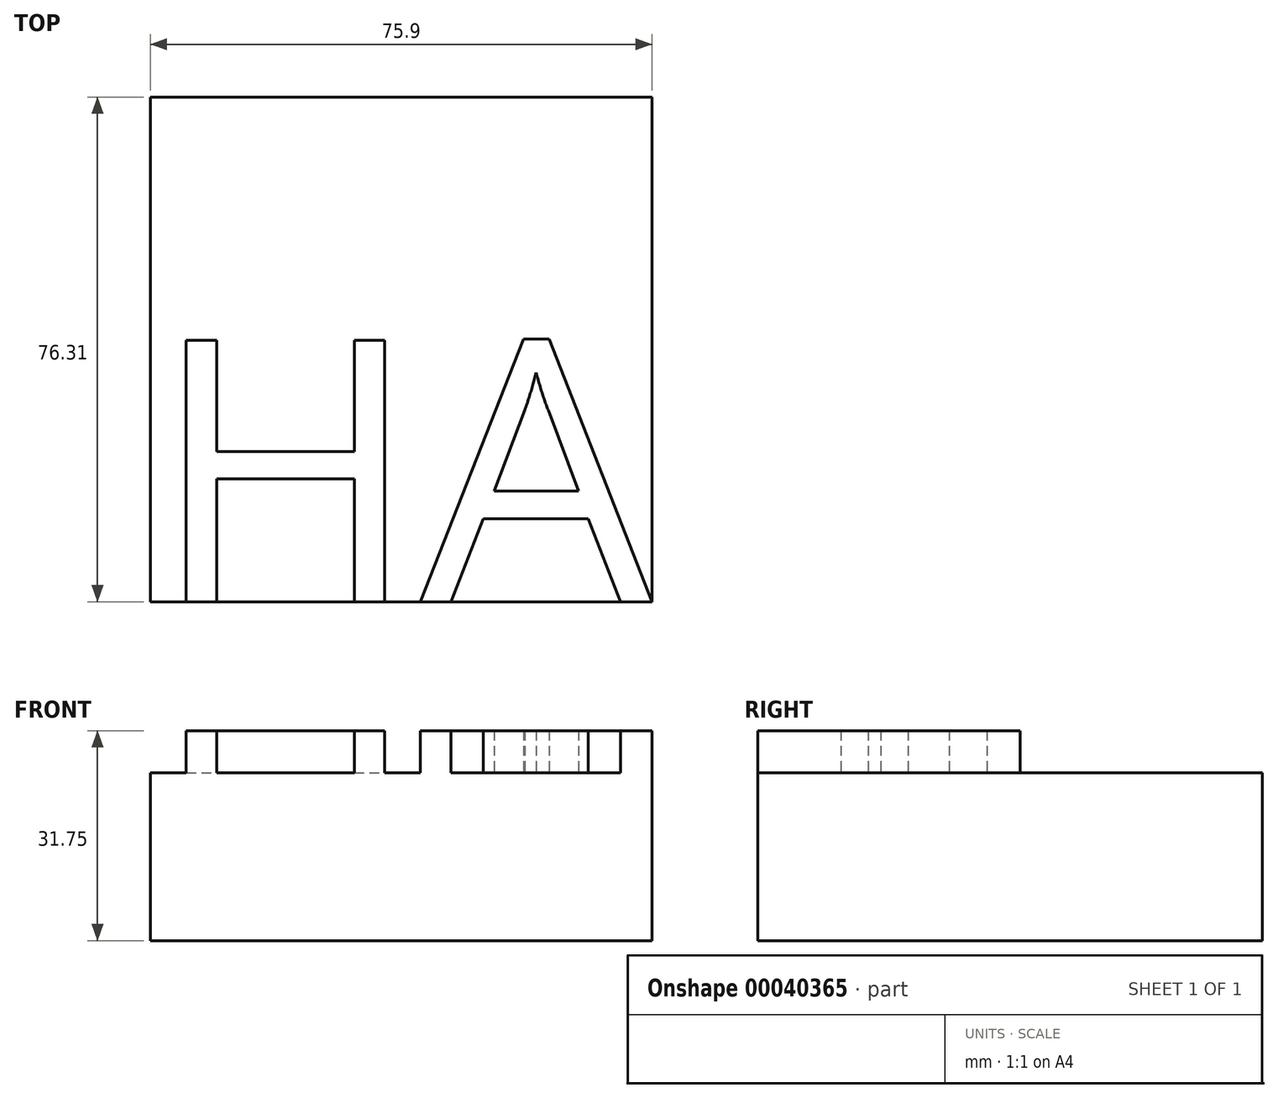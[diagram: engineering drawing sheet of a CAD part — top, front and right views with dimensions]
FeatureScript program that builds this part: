
annotation { "Feature Type Name" : "Feature", "Feature Type Description" : "" }
export const myFeature = defineFeature(function(context is Context, id is Id, definition is map)
    precondition{}
    {
        {
            var Q0;
            Q0=qCreatedBy(makeId("Top.planeOp"),FACE);
            var sketch = newSketch(context, id + "F0", { "sketchPlane" : qUnion([Q0])});
            skLineSegment(sketch, "E0.bottom", {"start": v(0, 0) * mm, "end": v(-75.9, 0) * mm});
            skLineSegment(sketch, "E0.top", {"start": v(0, 76.31) * mm, "end": v(-75.9, 76.31) * mm});
            skLineSegment(sketch, "E0.left", {"start": v(0, 0) * mm, "end": v(0, 76.31) * mm});
            skLineSegment(sketch, "E0.right", {"start": v(-75.9, 0) * mm, "end": v(-75.9, 76.31) * mm});
            skSolve(sketch);
        }
        {
            var Q0;
            Q0=makeQuery(id+"F0.imprint","IMPRINT",FACE,{"disambiguationData":[TD([[makeQuery(id+"F0.imprint","IMPRINT",EDGE,{"derivedFrom":sQuery(id+"F0.wireOp",EDGE,"E0.bottom")}),-1.0]])]});
            extrude(context, id + "F1", {"entities" : qUnion([Q0]), "depth" : 25.4 * mm});
        }
        {
            var Q0;
            Q0=makeQuery(id+"F1.opExtrude","CAP_FACE",FACE,{"disambiguationData":[OSD([sQuery(id+"F0.wireOp",EDGE,"E0.bottom"),sQuery(id+"F0.wireOp",EDGE,"E0.top"),sQuery(id+"F0.wireOp",EDGE,"E0.left"),sQuery(id+"F0.wireOp",EDGE,"E0.right")])],"isStart":false});
            var sketch = newSketch(context, id + "F2", { "sketchPlane" : qUnion([Q0])});
            skText(sketch, "E1", { "text": "HA", "fontName": "OpenSans-Regular.ttf"});
            const initialGuessF2  = {"E1": [-0.0759, 0, 1, 0, 0.03987]};
            skSetInitialGuess(sketch, initialGuessF2);
            skSolve(sketch);
        }
        {
            var Q0;
            Q0=makeQuery(id+"F2.imprint","IMPRINT",FACE,{"disambiguationData":[TD([[makeQuery(id+"F2.imprint","IMPRINT",EDGE,{"derivedFrom":sQuery(id+"F2.wireOp",EDGE,"E1.sketch_text.stroke-0")}),-1.0]])]});
            var Q1;
            Q1=makeQuery(id+"F2.imprint","IMPRINT",FACE,{"disambiguationData":[TD([[makeQuery(id+"F2.imprint","IMPRINT",EDGE,{"derivedFrom":sQuery(id+"F2.wireOp",EDGE,"E1.sketch_text.stroke-12")}),-1.0]])]});
            extrude(context, id + "F3", {"entities" : qUnion([Q0, Q1]), "operationType" : NewBodyOperationType.ADD, "depth" : 6.35 * mm});
        }
    });
